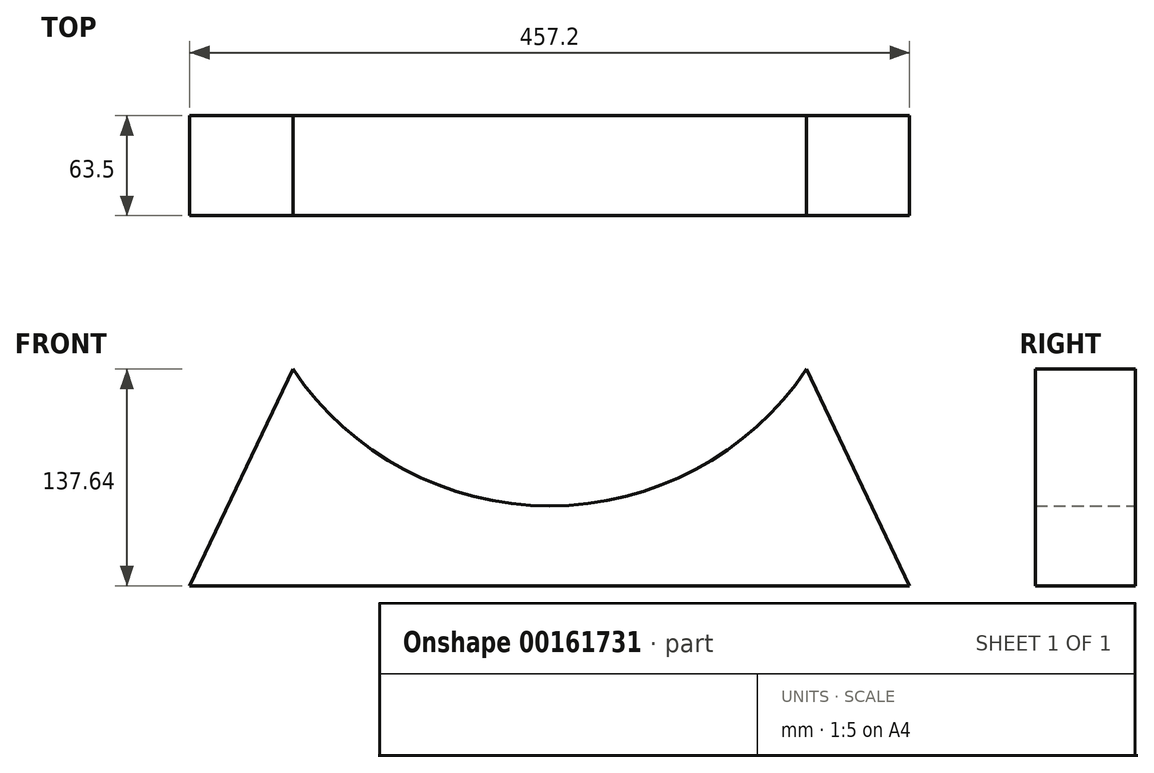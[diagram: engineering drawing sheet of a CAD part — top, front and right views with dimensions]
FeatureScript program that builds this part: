
annotation { "Feature Type Name" : "Feature", "Feature Type Description" : "" }
export const myFeature = defineFeature(function(context is Context, id is Id, definition is map)
    precondition{}
    {
        {
            var Q0;
            Q0=qCreatedBy(makeId("Front.planeOp"),FACE);
            var sketch = newSketch(context, id + "F0", { "sketchPlane" : qUnion([Q0])});
            skLineSegment(sketch, "E0", {"start": v(-228.6, 0) * mm, "end": v(228.6, 0) * mm});
            skLineSegment(sketch, "E1", {"start": v(228.6, 0) * mm, "end": v(163.18, 137.64) * mm});
            skLineSegment(sketch, "E2", {"start": v(-228.6, 0) * mm, "end": v(-163.18, 137.64) * mm});
            skArc(sketch, "E3", {"start": v(-163.18, 137.64) * mm, "mid": v(0, 50.8) * mm, "end": v(163.18, 137.64) * mm});
            skSolve(sketch);
        }
        {
            var Q0;
            Q0 = qSketchRegion(id + "F0", true);
            extrude(context, id + "F1", {"entities" : qUnion([Q0]), "depth" : 63.5 * mm});
        }
    });
